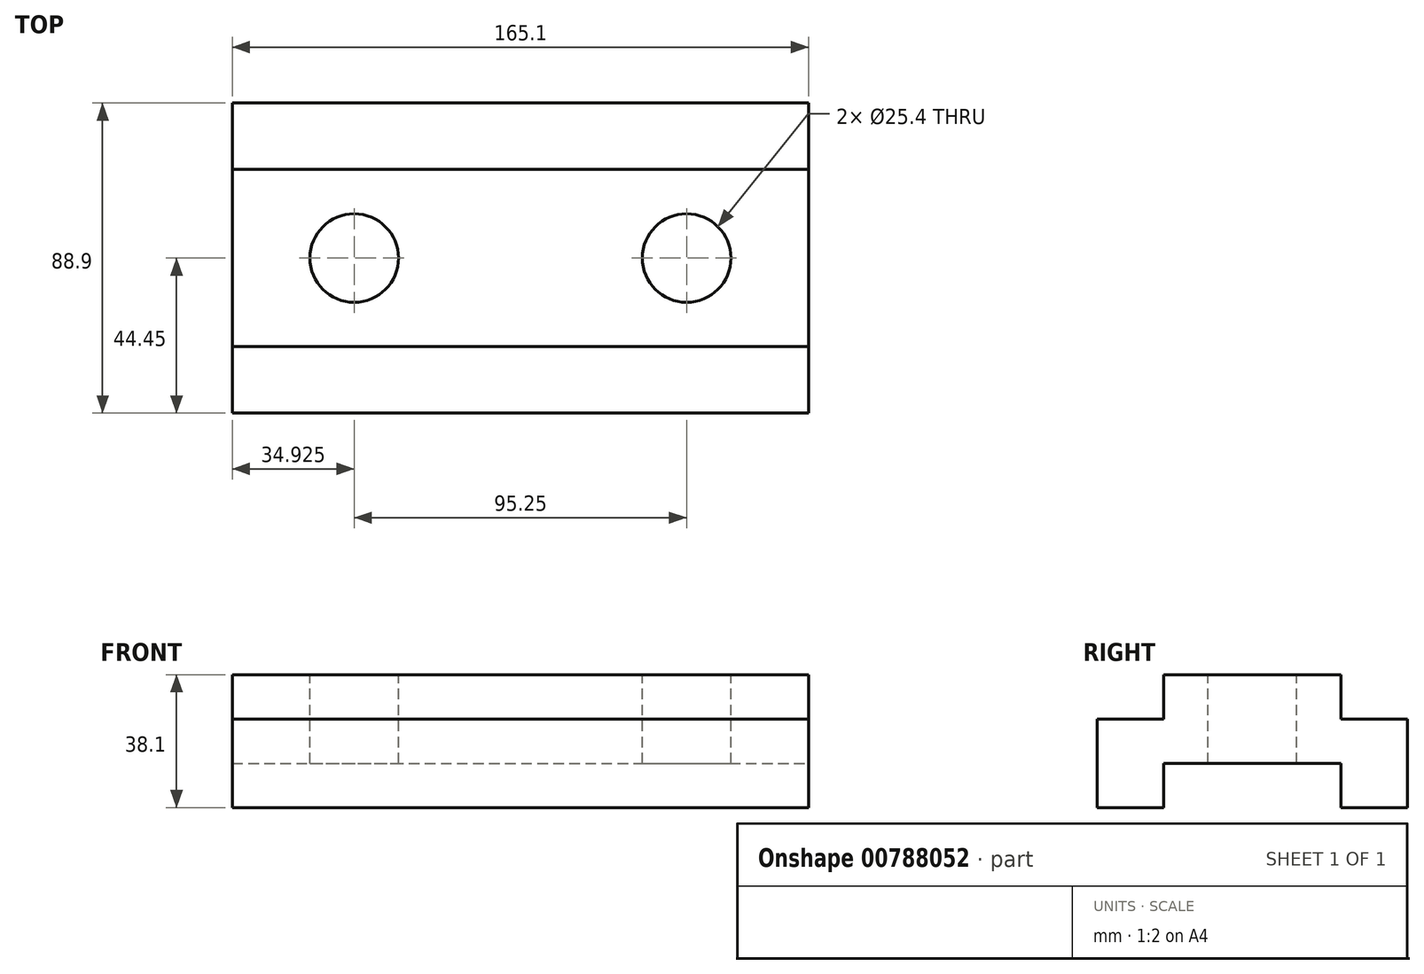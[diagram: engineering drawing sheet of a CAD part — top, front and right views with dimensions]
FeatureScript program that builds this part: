
annotation { "Feature Type Name" : "Feature", "Feature Type Description" : "" }
export const myFeature = defineFeature(function(context is Context, id is Id, definition is map)
    precondition{}
    {
        {
            var Q0;
            Q0=qCreatedBy(makeId("Front.planeOp"),FACE);
            var sketch = newSketch(context, id + "F0", { "sketchPlane" : qUnion([Q0])});
            skLineSegment(sketch, "E0", {"start": v(0, 0) * mm, "end": v(165.1, 0) * mm});
            skLineSegment(sketch, "E1", {"start": v(165.1, 0) * mm, "end": v(165.1, 38.1) * mm});
            skLineSegment(sketch, "E2", {"start": v(165.1, 38.1) * mm, "end": v(0, 38.1) * mm});
            skLineSegment(sketch, "E3", {"start": v(0, 38.1) * mm, "end": v(0, 0) * mm});
            skSolve(sketch);
        }
        {
            var Q0;
            Q0=makeQuery(id+"F0.imprint","IMPRINT",FACE,{"disambiguationData":[TD([[makeQuery(id+"F0.imprint","IMPRINT",EDGE,{"derivedFrom":sQuery(id+"F0.wireOp",EDGE,"E0")}),1.0]])]});
            extrude(context, id + "F1", {"entities" : qUnion([Q0]), "depth" : 88.9 * mm, "offsetDistance" : 25.4 * mm});
        }
        {
            var Q0;
            Q0=makeQuery(id+"F1.opExtrude","SWEPT_FACE",FACE,{"disambiguationData":[OSD([sQuery(id+"F0.wireOp",EDGE,"E1")])]});
            var sketch = newSketch(context, id + "F2", { "sketchPlane" : qUnion([Q0])});
            skLineSegment(sketch, "E4", {"start": v(-88.9, 0) * mm, "end": v(-69.85, 0) * mm});
            skLineSegment(sketch, "E5", {"start": v(-69.85, 0) * mm, "end": v(-19.05, 0) * mm});
            skLineSegment(sketch, "E6", {"start": v(-19.05, 0) * mm, "end": v(0, 0) * mm});
            skLineSegment(sketch, "E7", {"start": v(-69.85, 0) * mm, "end": v(-69.85, 12.7) * mm});
            skLineSegment(sketch, "E8", {"start": v(-69.85, 12.7) * mm, "end": v(-19.05, 12.7) * mm});
            skLineSegment(sketch, "E9", {"start": v(-19.05, 12.7) * mm, "end": v(-19.05, 0) * mm});
            skSolve(sketch);
        }
        {
            var Q0;
            Q0=makeQuery(id+"F2.imprint","IMPRINT",FACE,{"disambiguationData":[TD([[makeQuery(id+"F2.imprint","IMPRINT",EDGE,{"derivedFrom":sQuery(id+"F2.wireOp",EDGE,"E5")}),1.0]])]});
            extrude(context, id + "F3", {"entities" : qUnion([Q0]), "operationType" : NewBodyOperationType.REMOVE, "oppositeDirection" : true, "depth" : 165.1 * mm, "offsetDistance" : 25.4 * mm});
        }
        {
            var Q0;
            Q0=makeQuery(id+"F1.opExtrude","SWEPT_FACE",FACE,{"disambiguationData":[OSD([sQuery(id+"F0.wireOp",EDGE,"E2")])]});
            var sketch = newSketch(context, id + "F4", { "sketchPlane" : qUnion([Q0])});
            skLineSegment(sketch, "E10", {"start": v(0, -88.9) * mm, "end": v(0, -69.85) * mm});
            skLineSegment(sketch, "E11", {"start": v(0, -69.85) * mm, "end": v(0, -19.05) * mm});
            skLineSegment(sketch, "E12", {"start": v(0, -19.05) * mm, "end": v(0, 0) * mm});
            skLineSegment(sketch, "E13", {"start": v(0, -69.85) * mm, "end": v(165.1, -69.85) * mm});
            skLineSegment(sketch, "E14", {"start": v(165.1, -69.85) * mm, "end": v(165.1, -88.9) * mm});
            skLineSegment(sketch, "E15", {"start": v(165.1, -88.9) * mm, "end": v(0, -88.9) * mm});
            skLineSegment(sketch, "E16", {"start": v(0, -19.05) * mm, "end": v(165.1, -19.05) * mm});
            skLineSegment(sketch, "E17", {"start": v(165.1, -19.05) * mm, "end": v(165.1, 0) * mm});
            skLineSegment(sketch, "E18", {"start": v(165.1, 0) * mm, "end": v(0, 0) * mm});
            skLineSegment(sketch, "E19", {"start": v(165.1, -69.85) * mm, "end": v(165.1, -19.05) * mm});
            skSolve(sketch);
        }
        {
            var Q0;
            Q0=makeQuery(id+"F4.imprint","IMPRINT",FACE,{"disambiguationData":[TD([[makeQuery(id+"F4.imprint","IMPRINT",EDGE,{"derivedFrom":sQuery(id+"F4.wireOp",EDGE,"E10")}),-1.0]])]});
            extrude(context, id + "F5", {"entities" : qUnion([Q0]), "operationType" : NewBodyOperationType.REMOVE, "oppositeDirection" : true, "depth" : 12.7 * mm, "offsetDistance" : 25.4 * mm});
        }
        {
            var Q0;
            Q0=makeQuery(id+"F4.imprint","IMPRINT",FACE,{"disambiguationData":[TD([[makeQuery(id+"F4.imprint","IMPRINT",EDGE,{"derivedFrom":sQuery(id+"F4.wireOp",EDGE,"E12")}),-1.0]])]});
            extrude(context, id + "F6", {"entities" : qUnion([Q0]), "operationType" : NewBodyOperationType.REMOVE, "oppositeDirection" : true, "depth" : 12.7 * mm, "offsetDistance" : 25.4 * mm});
        }
        {
            var Q0;
            Q0=makeQuery(id+"F4.imprint","IMPRINT",FACE,{"disambiguationData":[TD([[makeQuery(id+"F4.imprint","IMPRINT",EDGE,{"derivedFrom":sQuery(id+"F4.wireOp",EDGE,"E11")}),-1.0]])]});
            var sketch = newSketch(context, id + "F7", { "sketchPlane" : qUnion([Q0])});
            skLineSegment(sketch, "E20", {"start": v(0, 0) * mm, "end": v(0, -44.45) * mm, "construction": true});
            skLineSegment(sketch, "E21", {"start": v(0, -44.45) * mm, "end": v(34.92, -44.45) * mm, "construction": true});
            skLineSegment(sketch, "E22", {"start": v(34.92, -44.45) * mm, "end": v(130.18, -44.45) * mm, "construction": true});
            skCircle(sketch, "E23", {"center": v(34.92, -44.45) * mm, "radius": 12.7 * mm});
            skCircle(sketch, "E24", {"center": v(130.18, -44.45) * mm, "radius": 12.7 * mm});
            skSolve(sketch);
        }
        {
            var Q0;
            Q0=makeQuery(id+"F7.imprint","IMPRINT",FACE,{"disambiguationData":[TD([[makeQuery(id+"F7.imprint","IMPRINT",EDGE,{"derivedFrom":sQuery(id+"F7.wireOp",EDGE,"E24")}),1.0]])]});
            extrude(context, id + "F8", {"entities" : qUnion([Q0]), "operationType" : NewBodyOperationType.REMOVE, "endBound" : BoundingType.UP_TO_NEXT, "oppositeDirection" : true, "depth" : 25.4 * mm, "offsetDistance" : 25.4 * mm});
        }
        {
            var Q0;
            Q0=makeQuery(id+"F7.imprint","IMPRINT",FACE,{"disambiguationData":[TD([[makeQuery(id+"F7.imprint","IMPRINT",EDGE,{"derivedFrom":sQuery(id+"F7.wireOp",EDGE,"E23")}),1.0]])]});
            extrude(context, id + "F9", {"entities" : qUnion([Q0]), "operationType" : NewBodyOperationType.REMOVE, "endBound" : BoundingType.UP_TO_NEXT, "oppositeDirection" : true, "depth" : 25.4 * mm, "offsetDistance" : 25.4 * mm});
        }
    });
